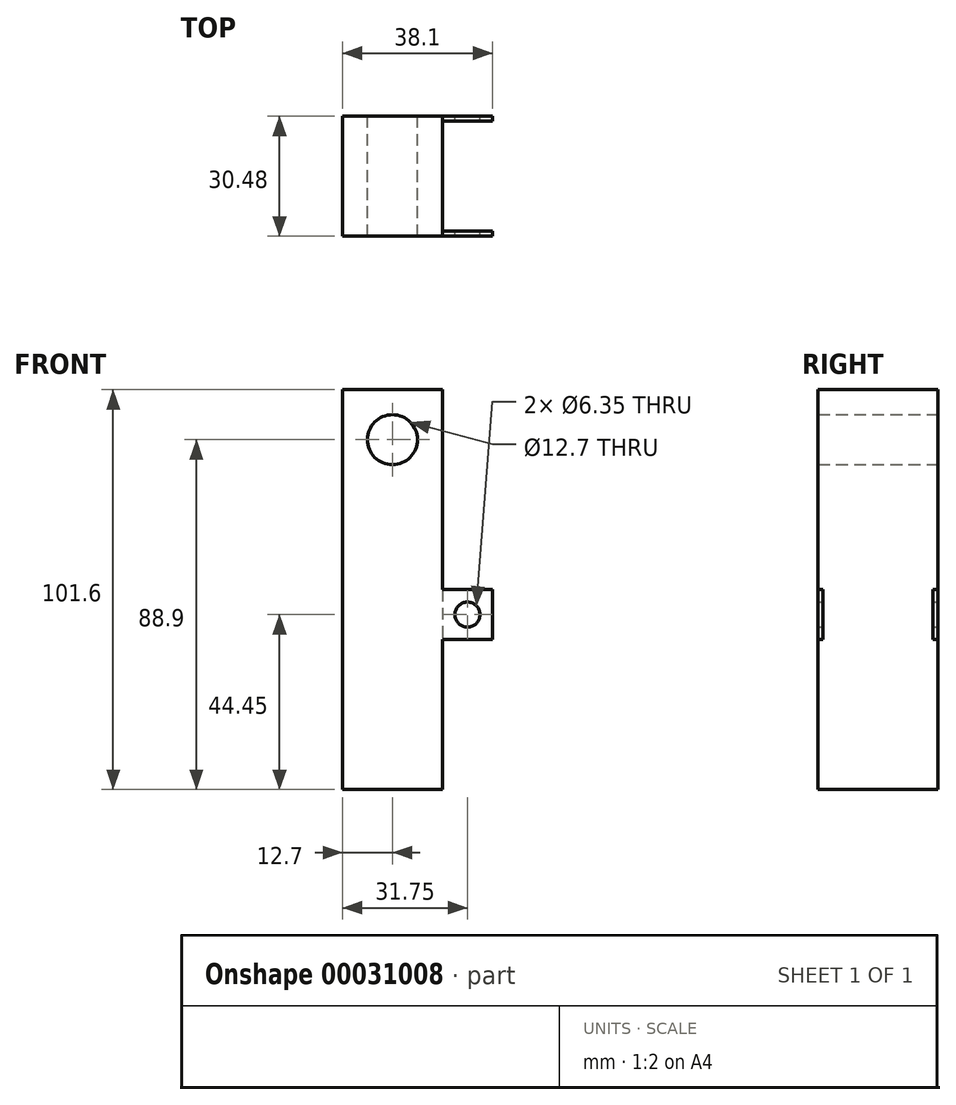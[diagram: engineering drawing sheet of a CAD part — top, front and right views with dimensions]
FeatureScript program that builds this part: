
annotation { "Feature Type Name" : "Feature", "Feature Type Description" : "" }
export const myFeature = defineFeature(function(context is Context, id is Id, definition is map)
    precondition{}
    {
        {
            var Q0;
            Q0=qCreatedBy(makeId("Front.planeOp"),FACE);
            var sketch = newSketch(context, id + "F0", { "sketchPlane" : qUnion([Q0])});
            skLineSegment(sketch, "E0.rect.bottom", {"start": v(-12.7, 50.8) * mm, "end": v(12.7, 50.8) * mm});
            skLineSegment(sketch, "E0.rect.top", {"start": v(-12.7, -50.8) * mm, "end": v(12.7, -50.8) * mm});
            skLineSegment(sketch, "E0.rect.left", {"start": v(-12.7, 50.8) * mm, "end": v(-12.7, -50.8) * mm});
            skLineSegment(sketch, "E0.rect.right", {"start": v(12.7, 50.8) * mm, "end": v(12.7, -50.8) * mm});
            skPoint(sketch, "E0.rect.middle", {"position": v(0, 0) * mm});
            skLineSegment(sketch, "E1.top", {"start": v(-12.7, 25.4) * mm, "end": v(12.7, 25.4) * mm});
            skLineSegment(sketch, "E1.left", {"start": v(-12.7, 50.8) * mm, "end": v(-12.7, 25.4) * mm});
            skLineSegment(sketch, "E1.right", {"start": v(12.7, 50.8) * mm, "end": v(12.7, 25.4) * mm});
            skCircle(sketch, "E2", {"center": v(0, 38.1) * mm, "radius": 6.35 * mm});
            skPoint(sketch, "E2.centerSnap0", {"position": v(0, 50.8) * mm});
            skPoint(sketch, "E2.centerSnap1", {"position": v(12.7, 38.1) * mm});
            skLineSegment(sketch, "E3.bottom", {"start": v(12.7, 0) * mm, "end": v(25.4, 0) * mm});
            skLineSegment(sketch, "E3.top", {"start": v(12.7, -12.7) * mm, "end": v(25.4, -12.7) * mm});
            skLineSegment(sketch, "E3.left", {"start": v(12.7, 0) * mm, "end": v(12.7, -12.7) * mm});
            skLineSegment(sketch, "E3.right", {"start": v(25.4, 0) * mm, "end": v(25.4, -12.7) * mm});
            skCircle(sketch, "E4", {"center": v(19.05, -6.35) * mm, "radius": 3.18 * mm});
            skPoint(sketch, "E4.centerSnap0", {"position": v(19.05, 0) * mm});
            skPoint(sketch, "E4.centerSnap1", {"position": v(25.4, -6.35) * mm});
            skSolve(sketch);
        }
        {
            var Q0;
            Q0=makeQuery(id+"F0.imprint","IMPRINT",FACE,{"disambiguationData":[TD([[makeQuery(id+"F0.imprint","IMPRINT",EDGE,{"derivedFrom":sQuery(id+"F0.wireOp",EDGE,"E0.rect.bottom")}),-1.0]])]});
            var Q1;
            {var subQ3=sQuery(id+"F0.wireOp",EDGE,"E0.rect.top");Q1=makeQuery(id+"F0.imprint","IMPRINT",FACE,{"disambiguationData":[TD([[makeQuery(id+"F0.imprint","IMPRINT",EDGE,{"derivedFrom":subQ3}),1.0]])]});}
            var Q2;
            Q2=makeQuery(id+"F0.imprint","IMPRINT",FACE,{"disambiguationData":[TD([[makeQuery(id+"F0.imprint","IMPRINT",EDGE,{"derivedFrom":sQuery(id+"F0.wireOp",EDGE,"E3.bottom")}),-1.0]])]});
            extrude(context, id + "F1", {"entities" : qUnion([Q0, Q1, Q2]), "depth" : 30.48 * mm});
        }
        {
            var Q0;
            Q0=makeQuery(id+"F1.opExtrude","SWEPT_FACE",FACE,{"disambiguationData":[OSD([sQuery(id+"F0.wireOp",EDGE,"E3.right")])]});
            var sketch = newSketch(context, id + "F2", { "sketchPlane" : qUnion([Q0])});
            skLineSegment(sketch, "E5", {"start": v(-33.02, 0) * mm, "end": v(-30.48, 0) * mm});
            skLineSegment(sketch, "E6.bottom", {"start": v(-29.21, 0) * mm, "end": v(-1.27, 0) * mm});
            skLineSegment(sketch, "E6.top", {"start": v(-29.21, -12.7) * mm, "end": v(-1.27, -12.7) * mm});
            skLineSegment(sketch, "E6.left", {"start": v(-29.21, 0) * mm, "end": v(-29.21, -12.7) * mm});
            skLineSegment(sketch, "E6.right", {"start": v(-1.27, 0) * mm, "end": v(-1.27, -12.7) * mm});
            skLineSegment(sketch, "E7", {"start": v(-30.48, 0) * mm, "end": v(-29.21, 0) * mm});
            skLineSegment(sketch, "E8", {"start": v(-1.27, 0) * mm, "end": v(0, 0) * mm});
            skSolve(sketch);
        }
        {
            var Q0;
            Q0=makeQuery(id+"F2.imprint","IMPRINT",FACE,{"disambiguationData":[TD([[makeQuery(id+"F2.imprint","IMPRINT",EDGE,{"derivedFrom":sQuery(id+"F2.wireOp",EDGE,"E6.top")}),1.0]])]});
            extrude(context, id + "F3", {"entities" : qUnion([Q0]), "operationType" : NewBodyOperationType.REMOVE, "oppositeDirection" : true, "depth" : 12.7 * mm});
        }
    });
